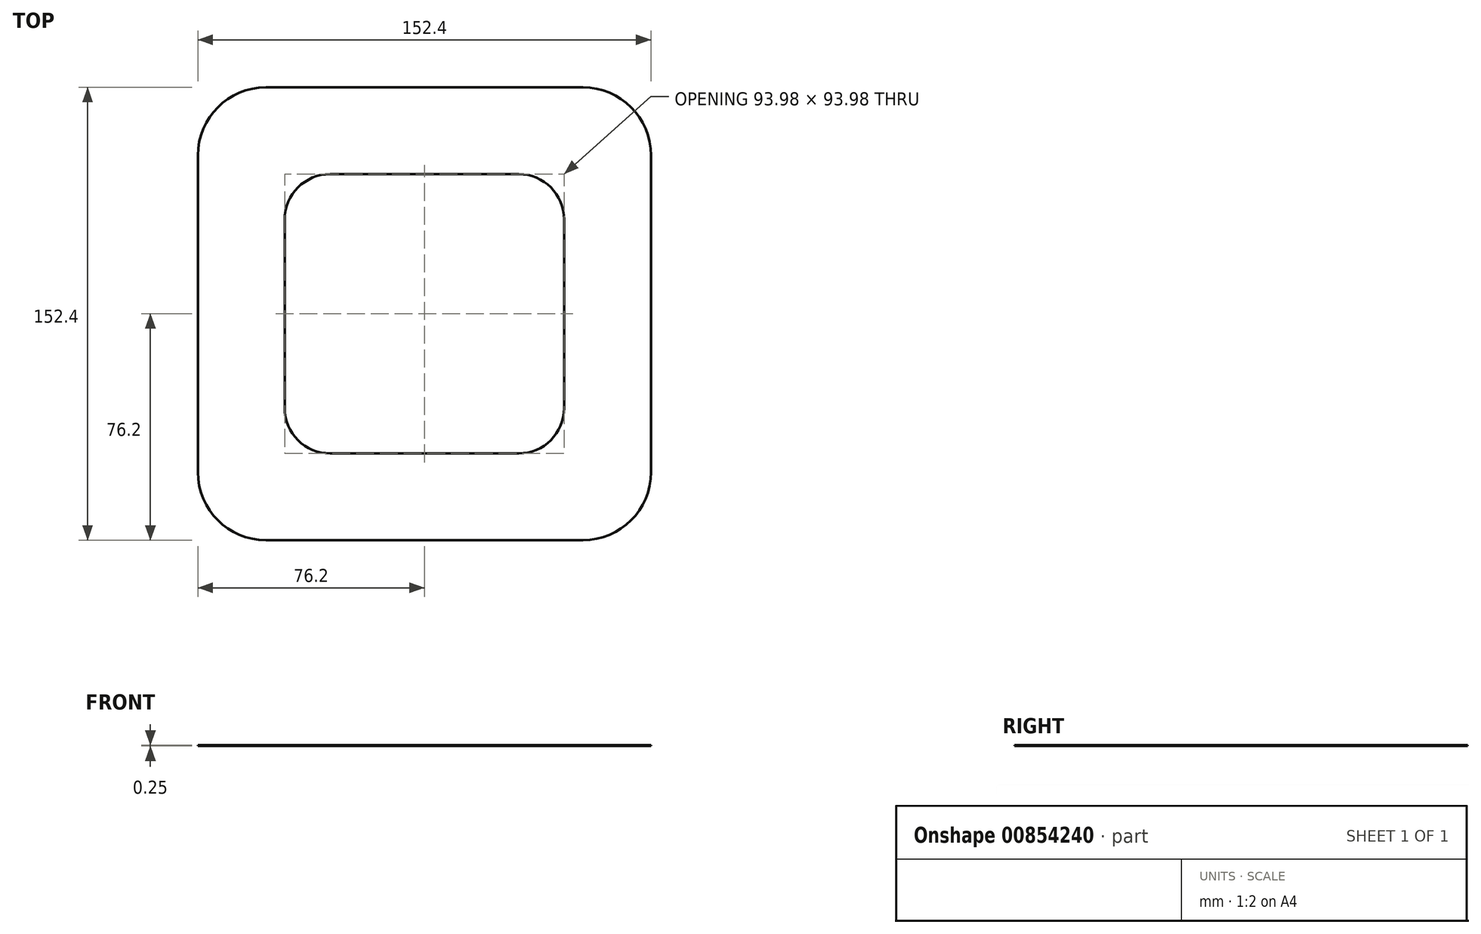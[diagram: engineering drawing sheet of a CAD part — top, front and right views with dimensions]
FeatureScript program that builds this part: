
annotation { "Feature Type Name" : "Feature", "Feature Type Description" : "" }
export const myFeature = defineFeature(function(context is Context, id is Id, definition is map)
    precondition{}
    {
        {
            var Q0;
            Q0=qCreatedBy(makeId("Top.planeOp"),FACE);
            var sketch = newSketch(context, id + "F0", { "sketchPlane" : qUnion([Q0])});
            skLineSegment(sketch, "E0.bottom", {"start": v(31.75, -46.99) * mm, "end": v(-31.75, -47) * mm});
            skLineSegment(sketch, "E0.top", {"start": v(31.75, 47) * mm, "end": v(-31.75, 46.99) * mm});
            skLineSegment(sketch, "E0.left", {"start": v(47, -31.75) * mm, "end": v(47, 31.75) * mm});
            skLineSegment(sketch, "E0.right", {"start": v(-47, -31.75) * mm, "end": v(-47, 31.75) * mm});
            skPoint(sketch, "E0.middle", {"position": v(0, 0) * mm});
            skPoint(sketch, "E1.visualSharp", {"position": v(-47, -47) * mm});
            skArc(sketch, "E1.filletArc", {"start": v(-47, -31.75) * mm, "mid": v(-42.53, -42.53) * mm, "end": v(-31.75, -47) * mm});
            skPoint(sketch, "E2.visualSharp", {"position": v(-47, 46.99) * mm});
            skArc(sketch, "E2.filletArc", {"start": v(-31.75, 46.99) * mm, "mid": v(-42.53, 42.53) * mm, "end": v(-47, 31.75) * mm});
            skPoint(sketch, "E3.visualSharp", {"position": v(47, 47) * mm});
            skArc(sketch, "E3.filletArc", {"start": v(47, 31.75) * mm, "mid": v(42.53, 42.53) * mm, "end": v(31.75, 47) * mm});
            skPoint(sketch, "E4.visualSharp", {"position": v(47, -46.99) * mm});
            skArc(sketch, "E4.filletArc", {"start": v(31.75, -46.99) * mm, "mid": v(42.53, -42.53) * mm, "end": v(47, -31.75) * mm});
            skLineSegment(sketch, "E5.bottom", {"start": v(53.34, -76.2) * mm, "end": v(-53.34, -76.2) * mm});
            skLineSegment(sketch, "E5.top", {"start": v(53.34, 76.2) * mm, "end": v(-53.34, 76.2) * mm});
            skLineSegment(sketch, "E5.left", {"start": v(76.2, -53.34) * mm, "end": v(76.2, 53.34) * mm});
            skLineSegment(sketch, "E5.right", {"start": v(-76.2, -53.34) * mm, "end": v(-76.2, 53.34) * mm});
            skPoint(sketch, "E6.visualSharp", {"position": v(-76.2, 76.2) * mm});
            skArc(sketch, "E6.filletArc", {"start": v(-53.34, 76.2) * mm, "mid": v(-69.5, 69.5) * mm, "end": v(-76.2, 53.34) * mm});
            skPoint(sketch, "E7.visualSharp", {"position": v(-76.2, -76.2) * mm});
            skArc(sketch, "E7.filletArc", {"start": v(-76.2, -53.34) * mm, "mid": v(-69.5, -69.5) * mm, "end": v(-53.34, -76.2) * mm});
            skPoint(sketch, "E8.visualSharp", {"position": v(76.2, -76.2) * mm});
            skArc(sketch, "E8.filletArc", {"start": v(53.34, -76.2) * mm, "mid": v(69.5, -69.5) * mm, "end": v(76.2, -53.34) * mm});
            skPoint(sketch, "E9.visualSharp", {"position": v(76.2, 76.2) * mm});
            skArc(sketch, "E9.filletArc", {"start": v(76.2, 53.34) * mm, "mid": v(69.5, 69.5) * mm, "end": v(53.34, 76.2) * mm});
            skSolve(sketch);
        }
        {
            var Q0;
            Q0=qSketchRegion(id+"F0",true);
            extrude(context, id + "F1", {"entities" : qUnion([Q0]), "depth" : 0.25 * mm});
        }
    });
